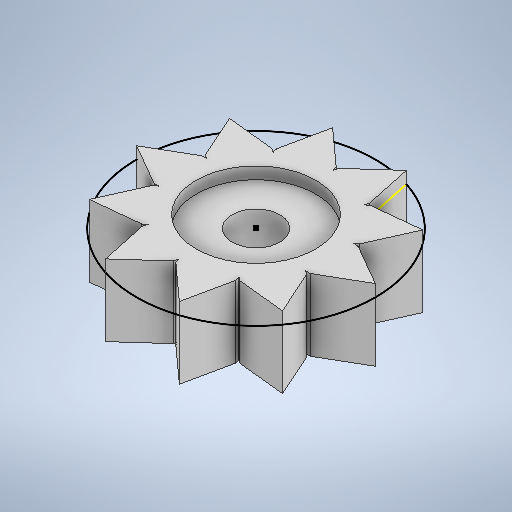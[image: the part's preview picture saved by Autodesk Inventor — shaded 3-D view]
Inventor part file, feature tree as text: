
AUTODESK INVENTOR PART (.ipt)
format: ipt  version: 2025.2 (Build 292293000, 293)  size: 311,296 bytes
history: native  units: mm
features: sketch x3, extrude x2, pattern_circular x1
ambient origin geometry x8: Origin, YZ Plane, XZ Plane, XY Plane, X Axis, Y Axis, Z Axis, Center Point
bodies: Solid1 (feature_tree)
feature tree (6):
  extrude  "Extrusion1"  Depth=45.0mm
  extrude  "Extrusion4"  Depth=20.0mm
  pattern_circular  "Circular Pattern2"  Count=2  [1 undecoded]
  sketch  "Sketch6"  dims[d5=5.0mm d6=5.0mm d7=5.0mm d8=5.0mm d9=2.0mm d10=0.0mm d27=10.0mm d28=5.0mm d29=2.0mm d30=10.0mm d31=2.0mm d32=30.0deg d33=2.0mm d34=30.0deg d35=0.5mm d36=2.5mm d37=0.0mm d38=0.0mm d39=100.0mm d40=360.0deg]
  sketch  "Sketch1"  dims[d0=50.0mm d1=45.0mm]
  sketch  "Sketch5"  dims[d2=4.5mm d3=20.0mm d4=20.0mm]
note: 1 required parameter value undecoded (feature->parameter linkage not recoverable at this tier; creation-order binding heuristic only, values carry confidence <= 0.55)
